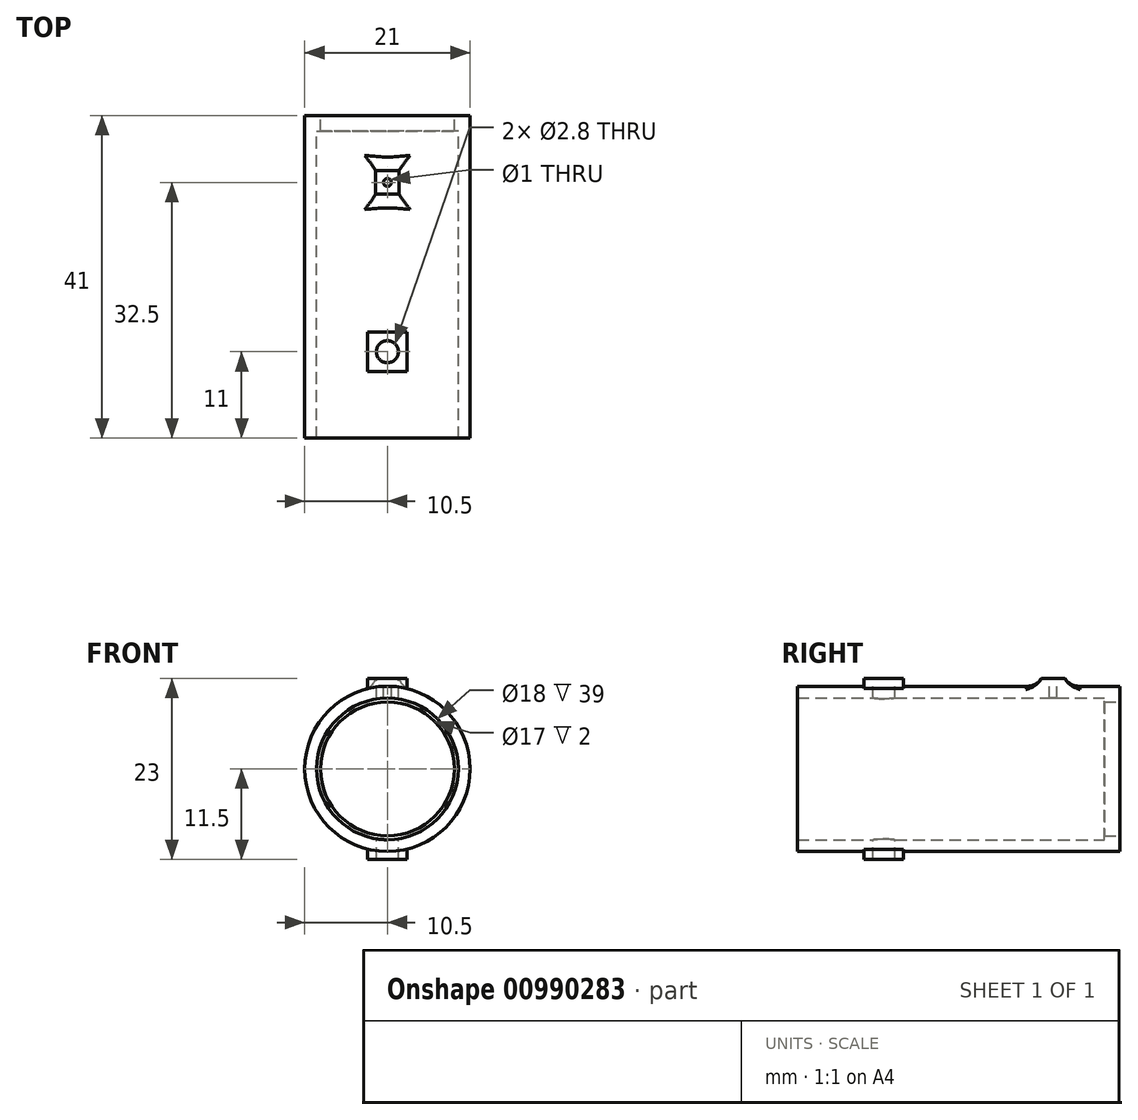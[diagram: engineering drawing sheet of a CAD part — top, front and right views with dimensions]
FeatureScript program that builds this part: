
annotation { "Feature Type Name" : "Feature", "Feature Type Description" : "" }
export const myFeature = defineFeature(function(context is Context, id is Id, definition is map)
    precondition{}
    {
        {
            var Q0;
            Q0=qCreatedBy(makeId("Front.planeOp"),FACE);
            var sketch = newSketch(context, id + "F0", { "sketchPlane" : qUnion([Q0])});
            skCircle(sketch, "E0", {"center": v(0, 0) * mm, "radius": 9 * mm});
            skCircle(sketch, "E1", {"center": v(0, 0) * mm, "radius": 10.5 * mm});
            skLineSegment(sketch, "E2.bottom", {"start": v(-2.5, 11.5) * mm, "end": v(2.5, 11.5) * mm});
            skLineSegment(sketch, "E2.top", {"start": v(-2.5, -11.5) * mm, "end": v(2.5, -11.5) * mm});
            skLineSegment(sketch, "E2.left", {"start": v(-2.5, 11.5) * mm, "end": v(-2.5, -11.5) * mm});
            skLineSegment(sketch, "E2.right", {"start": v(2.5, 11.5) * mm, "end": v(2.5, -11.5) * mm});
            skSolve(sketch);
        }
        {
            var Q0;
            Q0=qSketchRegion(id+"F0",true);
            extrude(context, id + "F1", {"entities" : qUnion([Q0]), "depth" : 41 * mm, "offsetDistance" : 25 * mm});
        }
        {
            var Q0;
            Q0=makeQuery(id+"F1.opExtrude","SWEPT_FACE",FACE,{"disambiguationData":[OSD([sQuery(id+"F0.wireOp",EDGE,"E2.bottom")])]});
            var sketch = newSketch(context, id + "F2", { "sketchPlane" : qUnion([Q0])});
            skCircle(sketch, "E3", {"center": v(0, -30) * mm, "radius": 1.4 * mm});
            skSolve(sketch);
        }
        {
            var Q0;
            Q0=qSketchRegion(id+"F2",true);
            extrude(context, id + "F3", {"entities" : qUnion([Q0]), "operationType" : NewBodyOperationType.REMOVE, "oppositeDirection" : true, "depth" : 25 * mm, "offsetDistance" : 25 * mm});
        }
        {
            var Q0;
            Q0=makeQuery(id+"F1.opExtrude","CAP_FACE",FACE,{"disambiguationData":[OSD([sQuery(id+"F0.wireOp",EDGE,"E0"),sQuery(id+"F0.wireOp",EDGE,"E1"),sQuery(id+"F0.wireOp",EDGE,"E2.bottom"),sQuery(id+"F0.wireOp",EDGE,"E2.top"),sQuery(id+"F0.wireOp",EDGE,"E2.left"),sQuery(id+"F0.wireOp",EDGE,"E2.right")])],"isStart":true});
            var sketch = newSketch(context, id + "F4", { "sketchPlane" : qUnion([Q0])});
            skCircle(sketch, "E4", {"center": v(0, 0) * mm, "radius": 8.5 * mm});
            skCircle(sketch, "E5", {"center": v(0, 0) * mm, "radius": 9 * mm});
            skSolve(sketch);
        }
        {
            var Q0;
            Q0=makeQuery(id+"F4.imprint","IMPRINT",FACE,{"disambiguationData":[TD([[makeQuery(id+"F4.imprint","IMPRINT",EDGE,{"derivedFrom":sQuery(id+"F4.wireOp",EDGE,"E4")}),-1.0]])]});
            extrude(context, id + "F5", {"entities" : qUnion([Q0]), "operationType" : NewBodyOperationType.ADD, "depth" : -2 * mm, "offsetDistance" : 25 * mm});
        }
        {
            var Q0;
            Q0=makeQuery(id+"F1.opExtrude","CAP_FACE",FACE,{"disambiguationData":[OSD([sQuery(id+"F0.wireOp",EDGE,"E0"),sQuery(id+"F0.wireOp",EDGE,"E1"),sQuery(id+"F0.wireOp",EDGE,"E2.bottom"),sQuery(id+"F0.wireOp",EDGE,"E2.top"),sQuery(id+"F0.wireOp",EDGE,"E2.left"),sQuery(id+"F0.wireOp",EDGE,"E2.right")])],"isStart":false});
            var sketch = newSketch(context, id + "F6", { "sketchPlane" : qUnion([Q0])});
            skArc(sketch, "E6", {"start": v(-2.5, 10.2) * mm, "mid": v(0, 10.5) * mm, "end": v(2.5, 10.2) * mm});
            skArc(sketch, "E7", {"start": v(2.5, -10.2) * mm, "mid": v(0, -10.5) * mm, "end": v(-2.5, -10.2) * mm});
            skLineSegment(sketch, "E8", {"start": v(-2.5, 10.2) * mm, "end": v(-2.5, 11.5) * mm});
            skLineSegment(sketch, "E9", {"start": v(-2.5, 11.5) * mm, "end": v(2.5, 11.5) * mm});
            skLineSegment(sketch, "E10", {"start": v(2.5, 11.5) * mm, "end": v(2.5, 10.2) * mm});
            skLineSegment(sketch, "E11", {"start": v(2.5, -10.2) * mm, "end": v(2.5, -11.5) * mm});
            skLineSegment(sketch, "E12", {"start": v(2.5, -11.5) * mm, "end": v(-2.5, -11.5) * mm});
            skLineSegment(sketch, "E13", {"start": v(-2.5, -11.5) * mm, "end": v(-2.5, -10.2) * mm});
            skSolve(sketch);
        }
        {
            var Q0;
            Q0=qSketchRegion(id+"F6",true);
            extrude(context, id + "F7", {"entities" : qUnion([Q0]), "operationType" : NewBodyOperationType.REMOVE, "oppositeDirection" : true, "depth" : 8.5 * mm, "offsetDistance" : 25 * mm});
        }
        {
            var Q0;
            Q0=makeQuery(id+"F5.boolean.opBoolean","MERGE",FACE,{"derivedFrom":[makeQuery(id+"F1.opExtrude","CAP_FACE",FACE,{"disambiguationData":[OSD([sQuery(id+"F0.wireOp",EDGE,"E0"),sQuery(id+"F0.wireOp",EDGE,"E1"),sQuery(id+"F0.wireOp",EDGE,"E2.bottom"),sQuery(id+"F0.wireOp",EDGE,"E2.top"),sQuery(id+"F0.wireOp",EDGE,"E2.left"),sQuery(id+"F0.wireOp",EDGE,"E2.right")])],"isStart":true}),makeQuery(id+"F5.opExtrude","CAP_FACE",FACE,{"disambiguationData":[OSD([sQuery(id+"F4.wireOp",EDGE,"E4"),sQuery(id+"F4.wireOp",EDGE,"E5")])],"isStart":true})]});
            var sketch = newSketch(context, id + "F8", { "sketchPlane" : qUnion([Q0])});
            skArc(sketch, "E14", {"start": v(-2.5, 10.2) * mm, "mid": v(0, 10.5) * mm, "end": v(2.5, 10.2) * mm});
            skArc(sketch, "E15", {"start": v(-2.5, -10.2) * mm, "mid": v(0, -10.5) * mm, "end": v(2.5, -10.2) * mm});
            skLineSegment(sketch, "E16", {"start": v(-2.5, 10.2) * mm, "end": v(-2.5, 11.5) * mm});
            skLineSegment(sketch, "E17", {"start": v(-2.5, 11.5) * mm, "end": v(2.5, 11.5) * mm});
            skLineSegment(sketch, "E18", {"start": v(2.5, 11.5) * mm, "end": v(2.5, 10.2) * mm});
            skLineSegment(sketch, "E19", {"start": v(2.5, -10.2) * mm, "end": v(2.5, -11.5) * mm});
            skLineSegment(sketch, "E20", {"start": v(2.5, -11.5) * mm, "end": v(-2.5, -11.5) * mm});
            skLineSegment(sketch, "E21", {"start": v(-2.5, -11.5) * mm, "end": v(-2.5, -10.2) * mm});
            skSolve(sketch);
        }
        {
            var Q0;
            Q0=qSketchRegion(id+"F8",true);
            extrude(context, id + "F9", {"entities" : qUnion([Q0]), "operationType" : NewBodyOperationType.REMOVE, "oppositeDirection" : true, "depth" : 27.5 * mm, "offsetDistance" : 25 * mm});
        }
        {
            var Q0;
            Q0=qCreatedBy(makeId("Top.planeOp"),FACE);
            cPlane(context, id + "F10", {"entities" : qUnion([Q0]), "cplaneType" : CPlaneType.OFFSET, "offset" : 10.5 * mm, "width" : 150 * mm, "height" : 150 * mm});
        }
        {
            var Q0;
            Q0=qCreatedBy(id+"F10.planeOp",FACE);
            var sketch = newSketch(context, id + "F11", { "sketchPlane" : qUnion([Q0])});
            skLineSegment(sketch, "E22.bottom", {"start": v(1.5, -10) * mm, "end": v(-1.5, -10) * mm});
            skLineSegment(sketch, "E22.top", {"start": v(1.5, -7) * mm, "end": v(-1.5, -7) * mm});
            skLineSegment(sketch, "E22.left", {"start": v(1.5, -10) * mm, "end": v(1.5, -7) * mm});
            skLineSegment(sketch, "E22.right", {"start": v(-1.5, -10) * mm, "end": v(-1.5, -7) * mm});
            skSolve(sketch);
        }
        {
            var Q0;
            Q0=qSketchRegion(id+"F11",true);
            extrude(context, id + "F12", {"entities" : qUnion([Q0]), "operationType" : NewBodyOperationType.ADD, "depth" : 1 * mm, "offsetDistance" : 25 * mm, "hasSecondDirection" : true, "secondDirectionOppositeDirection" : true, "secondDirectionDepth" : 1 * mm});
        }
        {
            var Q0;
            Q0=makeQuery(id+"F12.opExtrude","CAP_FACE",FACE,{"disambiguationData":[OSD([sQuery(id+"F11.wireOp",EDGE,"E22.bottom"),sQuery(id+"F11.wireOp",EDGE,"E22.top"),sQuery(id+"F11.wireOp",EDGE,"E22.left"),sQuery(id+"F11.wireOp",EDGE,"E22.right")])],"isStart":false});
            var sketch = newSketch(context, id + "F13", { "sketchPlane" : qUnion([Q0])});
            skCircle(sketch, "E23", {"center": v(0, -8.5) * mm, "radius": 0.5 * mm});
            skSolve(sketch);
        }
        {
            var Q0;
            {var subQ0=sQuery(id+"F0.wireOp",EDGE,"E2.right");var subQ1=sQuery(id+"F0.wireOp",EDGE,"E1");var subQ2=sQuery(id+"F0.wireOp",EDGE,"E2.left");Q0=makeQuery(id+"F12.boolean.opBoolean","INTERSECT",EDGE,{"derivedFrom":[makeQuery(id+"F9.boolean.opBoolean","MERGE",FACE,{"derivedFrom":[makeQuery(id+"F7.boolean.opBoolean","MERGE",FACE,{"derivedFrom":[makeQuery(id+"F1.opExtrude","SWEPT_FACE",FACE,{"disambiguationData":[OSD([subQ1]),TDD([makeQuery(id+"F0.imprint","IMPRINT",EDGE,{"disambiguationData":[TD([[makeQuery(id+"F0.imprint","INTERSECT",VERTEX,{"disambiguationData":[OD(0.0)],"derivedFrom":[subQ1,subQ2]}),-1.0]])],"derivedFrom":subQ1})])]}),makeQuery(id+"F1.opExtrude","SWEPT_FACE",FACE,{"disambiguationData":[OSD([subQ1]),TDD([makeQuery(id+"F0.imprint","IMPRINT",EDGE,{"disambiguationData":[TD([[makeQuery(id+"F0.imprint","INTERSECT",VERTEX,{"disambiguationData":[OD(0.0)],"derivedFrom":[subQ1,subQ0]}),1.0]])],"derivedFrom":subQ1})])]})],"fromTools":[makeQuery(id+"F7.opExtrude","SWEPT_FACE",FACE,{"disambiguationData":[OSD([sQuery(id+"F6.wireOp",EDGE,"E6")])]}),makeQuery(id+"F7.opExtrude","SWEPT_FACE",FACE,{"disambiguationData":[OSD([sQuery(id+"F6.wireOp",EDGE,"E7")])]})]})],"fromTools":[makeQuery(id+"F9.opExtrude","SWEPT_FACE",FACE,{"disambiguationData":[OSD([sQuery(id+"F8.wireOp",EDGE,"E14")])]}),makeQuery(id+"F9.opExtrude","SWEPT_FACE",FACE,{"disambiguationData":[OSD([sQuery(id+"F8.wireOp",EDGE,"E15")])]})]}),makeQuery(id+"F12.opExtrude","SWEPT_FACE",FACE,{"disambiguationData":[OSD([sQuery(id+"F11.wireOp",EDGE,"E22.left")])]})]});}
            var Q1;
            {var subQ0=sQuery(id+"F0.wireOp",EDGE,"E2.right");var subQ1=sQuery(id+"F0.wireOp",EDGE,"E1");var subQ2=sQuery(id+"F0.wireOp",EDGE,"E2.left");Q1=makeQuery(id+"F12.boolean.opBoolean","INTERSECT",EDGE,{"derivedFrom":[makeQuery(id+"F9.boolean.opBoolean","MERGE",FACE,{"derivedFrom":[makeQuery(id+"F7.boolean.opBoolean","MERGE",FACE,{"derivedFrom":[makeQuery(id+"F1.opExtrude","SWEPT_FACE",FACE,{"disambiguationData":[OSD([subQ1]),TDD([makeQuery(id+"F0.imprint","IMPRINT",EDGE,{"disambiguationData":[TD([[makeQuery(id+"F0.imprint","INTERSECT",VERTEX,{"disambiguationData":[OD(0.0)],"derivedFrom":[subQ1,subQ2]}),-1.0]])],"derivedFrom":subQ1})])]}),makeQuery(id+"F1.opExtrude","SWEPT_FACE",FACE,{"disambiguationData":[OSD([subQ1]),TDD([makeQuery(id+"F0.imprint","IMPRINT",EDGE,{"disambiguationData":[TD([[makeQuery(id+"F0.imprint","INTERSECT",VERTEX,{"disambiguationData":[OD(0.0)],"derivedFrom":[subQ1,subQ0]}),1.0]])],"derivedFrom":subQ1})])]})],"fromTools":[makeQuery(id+"F7.opExtrude","SWEPT_FACE",FACE,{"disambiguationData":[OSD([sQuery(id+"F6.wireOp",EDGE,"E6")])]}),makeQuery(id+"F7.opExtrude","SWEPT_FACE",FACE,{"disambiguationData":[OSD([sQuery(id+"F6.wireOp",EDGE,"E7")])]})]})],"fromTools":[makeQuery(id+"F9.opExtrude","SWEPT_FACE",FACE,{"disambiguationData":[OSD([sQuery(id+"F8.wireOp",EDGE,"E14")])]}),makeQuery(id+"F9.opExtrude","SWEPT_FACE",FACE,{"disambiguationData":[OSD([sQuery(id+"F8.wireOp",EDGE,"E15")])]})]}),makeQuery(id+"F12.opExtrude","SWEPT_FACE",FACE,{"disambiguationData":[OSD([sQuery(id+"F11.wireOp",EDGE,"E22.right")])]})]});}
            var Q2;
            {var subQ0=sQuery(id+"F0.wireOp",EDGE,"E2.right");var subQ1=sQuery(id+"F0.wireOp",EDGE,"E1");var subQ2=sQuery(id+"F0.wireOp",EDGE,"E2.left");Q2=makeQuery(id+"F12.boolean.opBoolean","INTERSECT",EDGE,{"derivedFrom":[makeQuery(id+"F9.boolean.opBoolean","MERGE",FACE,{"derivedFrom":[makeQuery(id+"F7.boolean.opBoolean","MERGE",FACE,{"derivedFrom":[makeQuery(id+"F1.opExtrude","SWEPT_FACE",FACE,{"disambiguationData":[OSD([subQ1]),TDD([makeQuery(id+"F0.imprint","IMPRINT",EDGE,{"disambiguationData":[TD([[makeQuery(id+"F0.imprint","INTERSECT",VERTEX,{"disambiguationData":[OD(0.0)],"derivedFrom":[subQ1,subQ2]}),-1.0]])],"derivedFrom":subQ1})])]}),makeQuery(id+"F1.opExtrude","SWEPT_FACE",FACE,{"disambiguationData":[OSD([subQ1]),TDD([makeQuery(id+"F0.imprint","IMPRINT",EDGE,{"disambiguationData":[TD([[makeQuery(id+"F0.imprint","INTERSECT",VERTEX,{"disambiguationData":[OD(0.0)],"derivedFrom":[subQ1,subQ0]}),1.0]])],"derivedFrom":subQ1})])]})],"fromTools":[makeQuery(id+"F7.opExtrude","SWEPT_FACE",FACE,{"disambiguationData":[OSD([sQuery(id+"F6.wireOp",EDGE,"E6")])]}),makeQuery(id+"F7.opExtrude","SWEPT_FACE",FACE,{"disambiguationData":[OSD([sQuery(id+"F6.wireOp",EDGE,"E7")])]})]})],"fromTools":[makeQuery(id+"F9.opExtrude","SWEPT_FACE",FACE,{"disambiguationData":[OSD([sQuery(id+"F8.wireOp",EDGE,"E14")])]}),makeQuery(id+"F9.opExtrude","SWEPT_FACE",FACE,{"disambiguationData":[OSD([sQuery(id+"F8.wireOp",EDGE,"E15")])]})]}),makeQuery(id+"F12.opExtrude","SWEPT_FACE",FACE,{"disambiguationData":[OSD([sQuery(id+"F11.wireOp",EDGE,"E22.top")])]})]});}
            var Q3;
            {var subQ0=sQuery(id+"F0.wireOp",EDGE,"E2.right");var subQ1=sQuery(id+"F0.wireOp",EDGE,"E1");var subQ2=sQuery(id+"F0.wireOp",EDGE,"E2.left");Q3=makeQuery(id+"F12.boolean.opBoolean","INTERSECT",EDGE,{"derivedFrom":[makeQuery(id+"F9.boolean.opBoolean","MERGE",FACE,{"derivedFrom":[makeQuery(id+"F7.boolean.opBoolean","MERGE",FACE,{"derivedFrom":[makeQuery(id+"F1.opExtrude","SWEPT_FACE",FACE,{"disambiguationData":[OSD([subQ1]),TDD([makeQuery(id+"F0.imprint","IMPRINT",EDGE,{"disambiguationData":[TD([[makeQuery(id+"F0.imprint","INTERSECT",VERTEX,{"disambiguationData":[OD(0.0)],"derivedFrom":[subQ1,subQ2]}),-1.0]])],"derivedFrom":subQ1})])]}),makeQuery(id+"F1.opExtrude","SWEPT_FACE",FACE,{"disambiguationData":[OSD([subQ1]),TDD([makeQuery(id+"F0.imprint","IMPRINT",EDGE,{"disambiguationData":[TD([[makeQuery(id+"F0.imprint","INTERSECT",VERTEX,{"disambiguationData":[OD(0.0)],"derivedFrom":[subQ1,subQ0]}),1.0]])],"derivedFrom":subQ1})])]})],"fromTools":[makeQuery(id+"F7.opExtrude","SWEPT_FACE",FACE,{"disambiguationData":[OSD([sQuery(id+"F6.wireOp",EDGE,"E6")])]}),makeQuery(id+"F7.opExtrude","SWEPT_FACE",FACE,{"disambiguationData":[OSD([sQuery(id+"F6.wireOp",EDGE,"E7")])]})]})],"fromTools":[makeQuery(id+"F9.opExtrude","SWEPT_FACE",FACE,{"disambiguationData":[OSD([sQuery(id+"F8.wireOp",EDGE,"E14")])]}),makeQuery(id+"F9.opExtrude","SWEPT_FACE",FACE,{"disambiguationData":[OSD([sQuery(id+"F8.wireOp",EDGE,"E15")])]})]}),makeQuery(id+"F12.opExtrude","SWEPT_FACE",FACE,{"disambiguationData":[OSD([sQuery(id+"F11.wireOp",EDGE,"E22.bottom")])]})]});}
            fillet(context, id + "F14", {"entities" : qUnion([Q0, Q1, Q2, Q3]), "radius" : 2 * mm, "tangentPropagation" : true, "allowEdgeOverflow" : false});
        }
        {
            var Q0;
            Q0=qSketchRegion(id+"F13",true);
            extrude(context, id + "F15", {"entities" : qUnion([Q0]), "operationType" : NewBodyOperationType.REMOVE, "oppositeDirection" : true, "depth" : 3 * mm, "offsetDistance" : 25 * mm});
        }
    });
